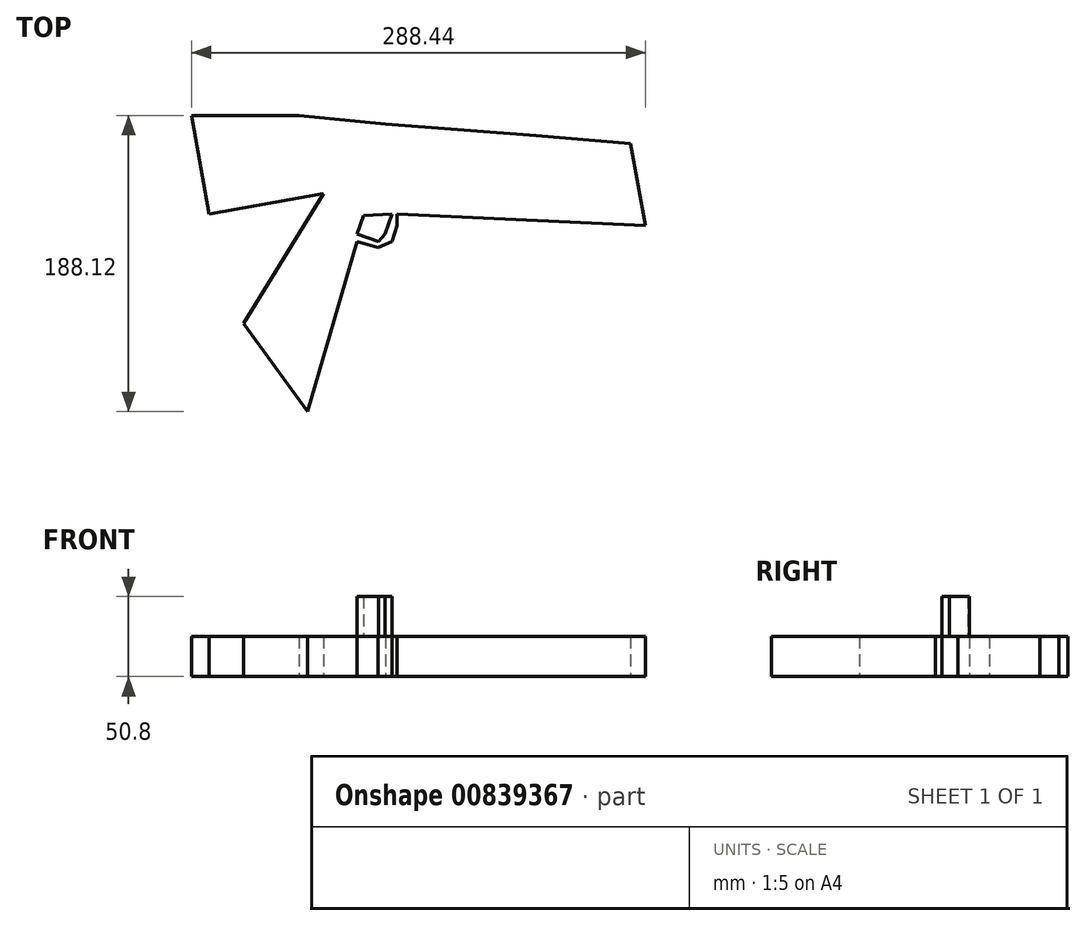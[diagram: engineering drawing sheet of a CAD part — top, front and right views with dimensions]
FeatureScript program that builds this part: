
annotation { "Feature Type Name" : "Feature", "Feature Type Description" : "" }
export const myFeature = defineFeature(function(context is Context, id is Id, definition is map)
    precondition{}
    {
        {
            var Q0;
            Q0=qCreatedBy(makeId("Top.planeOp"),FACE);
            var sketch = newSketch(context, id + "F0", { "sketchPlane" : qUnion([Q0])});
            skLineSegment(sketch, "E0", {"start": v(-98.39, 25.52) * mm, "end": v(-149.03, -57.08) * mm});
            skLineSegment(sketch, "E1", {"start": v(-149.03, -57.08) * mm, "end": v(-108.42, -112.9) * mm});
            skLineSegment(sketch, "E2", {"start": v(-108.42, -112.9) * mm, "end": v(-77.05, -4.85) * mm});
            skLineSegment(sketch, "E3", {"start": v(-77.05, -4.85) * mm, "end": v(-63.58, -8.76) * mm});
            skLineSegment(sketch, "E4", {"start": v(-63.58, -8.76) * mm, "end": v(-54.7, -4.85) * mm});
            skLineSegment(sketch, "E5", {"start": v(-54.7, -4.85) * mm, "end": v(-51.75, 5.33) * mm});
            skLineSegment(sketch, "E6", {"start": v(-77.05, -4.85) * mm, "end": v(-74.1, 5.33) * mm});
            skLineSegment(sketch, "E7", {"start": v(-74.1, 5.33) * mm, "end": v(-51.75, 5.33) * mm});
            skLineSegment(sketch, "E8", {"start": v(-98.39, 25.52) * mm, "end": v(-170.96, 12.59) * mm});
            skLineSegment(sketch, "E9", {"start": v(-170.96, 12.59) * mm, "end": v(-182.12, 75.22) * mm});
            skLineSegment(sketch, "E10", {"start": v(-182.12, 75.22) * mm, "end": v(-113.76, 75.22) * mm});
            skLineSegment(sketch, "E11", {"start": v(-113.76, 75.22) * mm, "end": v(-59.04, 69.58) * mm});
            skLineSegment(sketch, "E12", {"start": v(-59.04, 69.58) * mm, "end": v(36.63, 62.3) * mm});
            skLineSegment(sketch, "E13", {"start": v(36.63, 62.3) * mm, "end": v(96.67, 57.34) * mm});
            skLineSegment(sketch, "E14", {"start": v(96.67, 57.34) * mm, "end": v(106.32, 5.33) * mm});
            skLineSegment(sketch, "E15", {"start": v(106.32, 5.33) * mm, "end": v(-51.75, 12.59) * mm});
            skLineSegment(sketch, "E16", {"start": v(-51.75, 12.59) * mm, "end": v(-51.75, 5.33) * mm});
            skSolve(sketch);
        }
        {
            var Q0;
            Q0 = qSketchRegion(id + "F0", true);
            extrude(context, id + "F1", {"entities" : qUnion([Q0]), "depth" : 25.4 * mm, "offsetDistance" : 25.4 * mm});
        }
        {
            var Q0;
            Q0=makeQuery(id+"F1.opExtrude","CAP_FACE",FACE,{"disambiguationData":[OSD([sQuery(id+"F0.wireOp",EDGE,"E0"),sQuery(id+"F0.wireOp",EDGE,"E1"),sQuery(id+"F0.wireOp",EDGE,"E2"),sQuery(id+"F0.wireOp",EDGE,"E3"),sQuery(id+"F0.wireOp",EDGE,"E4"),sQuery(id+"F0.wireOp",EDGE,"E5"),sQuery(id+"F0.wireOp",EDGE,"E8"),sQuery(id+"F0.wireOp",EDGE,"E9"),sQuery(id+"F0.wireOp",EDGE,"E10"),sQuery(id+"F0.wireOp",EDGE,"E11"),sQuery(id+"F0.wireOp",EDGE,"E12"),sQuery(id+"F0.wireOp",EDGE,"E13"),sQuery(id+"F0.wireOp",EDGE,"E14"),sQuery(id+"F0.wireOp",EDGE,"E15"),sQuery(id+"F0.wireOp",EDGE,"E16")])],"isStart":false});
            var sketch = newSketch(context, id + "F2", { "sketchPlane" : qUnion([Q0])});
            skLineSegment(sketch, "E17", {"start": v(-72.9, 11.73) * mm, "end": v(-77.05, 0) * mm});
            skLineSegment(sketch, "E18", {"start": v(-77.05, 0) * mm, "end": v(-63.35, -4.85) * mm});
            skLineSegment(sketch, "E19", {"start": v(-63.35, -4.85) * mm, "end": v(-59.14, 0) * mm});
            skPoint(sketch, "E19.endSnap0", {"position": v(-59.14, -6.8) * mm});
            skLineSegment(sketch, "E20", {"start": v(-59.14, 0) * mm, "end": v(-54.7, 12.59) * mm});
            skLineSegment(sketch, "E21", {"start": v(-54.7, 12.59) * mm, "end": v(-72.9, 11.73) * mm});
            skSolve(sketch);
        }
        {
            var Q0;
            Q0 = qSketchRegion(id + "F2", true);
            extrude(context, id + "F3", {"entities" : qUnion([Q0]), "operationType" : NewBodyOperationType.ADD, "depth" : 25.4 * mm, "offsetDistance" : 25.4 * mm});
        }
    });
